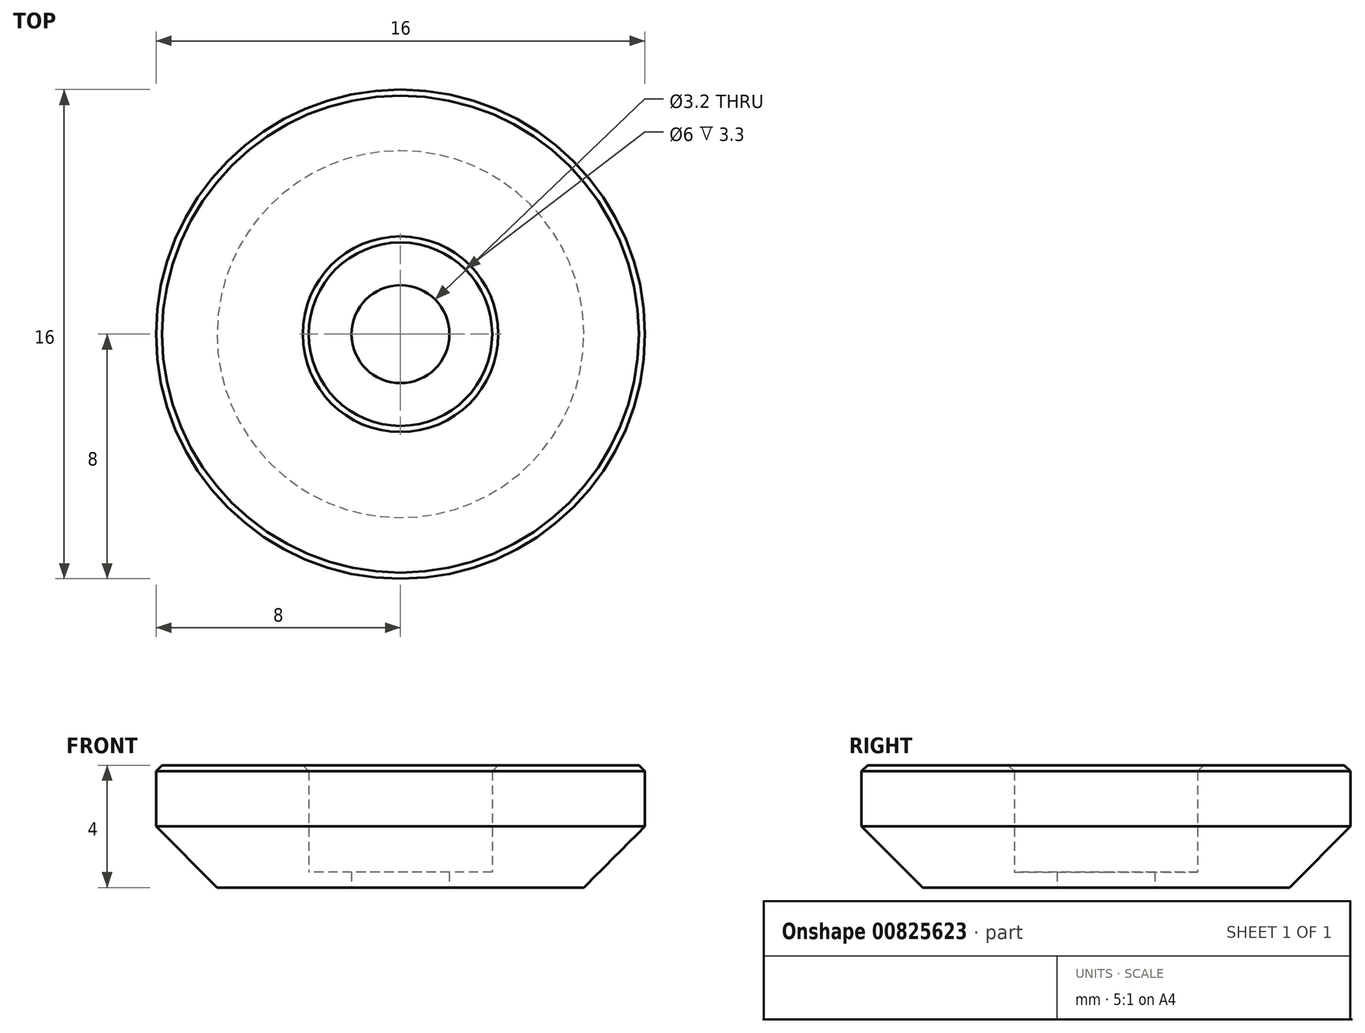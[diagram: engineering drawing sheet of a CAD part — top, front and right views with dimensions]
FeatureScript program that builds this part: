
annotation { "Feature Type Name" : "Feature", "Feature Type Description" : "" }
export const myFeature = defineFeature(function(context is Context, id is Id, definition is map)
    precondition{}
    {
        {
            var Q0;
            Q0=qCreatedBy(makeId("Top.planeOp"),FACE);
            var sketch = newSketch(context, id + "F0", { "sketchPlane" : qUnion([Q0])});
            skCircle(sketch, "E0", {"center": v(0, 0) * mm, "radius": 3 * mm});
            skCircle(sketch, "E1", {"center": v(0, 0) * mm, "radius": 1.6 * mm});
            skCircle(sketch, "E2", {"center": v(0, 0) * mm, "radius": 8 * mm});
            skSolve(sketch);
        }
        {
            var Q0;
            Q0=makeQuery(id+"F0.imprint","IMPRINT",FACE,{"disambiguationData":[TD([[makeQuery(id+"F0.imprint","IMPRINT",EDGE,{"derivedFrom":sQuery(id+"F0.wireOp",EDGE,"E0")}),1.0]])]});
            extrude(context, id + "F1", {"entities" : qUnion([Q0]), "depth" : 0.5 * mm, "offsetDistance" : 25 * mm});
        }
        {
            var Q0;
            Q0=makeQuery(id+"F0.imprint","IMPRINT",FACE,{"disambiguationData":[TD([[makeQuery(id+"F0.imprint","IMPRINT",EDGE,{"derivedFrom":sQuery(id+"F0.wireOp",EDGE,"E0")}),-1.0]])]});
            extrude(context, id + "F2", {"entities" : qUnion([Q0]), "operationType" : NewBodyOperationType.ADD, "depth" : 4 * mm, "offsetDistance" : 25 * mm});
        }
        {
            var Q0;
            Q0=makeQuery(id+"F2.opExtrude","CAP_EDGE",EDGE,{"disambiguationData":[OSD([sQuery(id+"F0.wireOp",EDGE,"E2")])],"isStart":true});
            chamfer(context, id + "F3", {"entities" : qUnion([Q0]), "width" : 2 * mm, "tangentPropagation" : true});
        }
        {
            var Q0;
            Q0=makeQuery(id+"F2.opExtrude","CAP_EDGE",EDGE,{"disambiguationData":[OSD([sQuery(id+"F0.wireOp",EDGE,"E2")])],"isStart":false});
            var Q1;
            Q1=makeQuery(id+"F2.opExtrude","CAP_EDGE",EDGE,{"disambiguationData":[OSD([sQuery(id+"F0.wireOp",EDGE,"E0")])],"isStart":false});
            var Q2;
            Q2=makeQuery(id+"F1.opExtrude","CAP_EDGE",EDGE,{"disambiguationData":[OSD([sQuery(id+"F0.wireOp",EDGE,"E0")])],"isStart":false});
            chamfer(context, id + "F4", {"entities" : qUnion([Q0, Q1, Q2]), "width" : 0.2 * mm, "tangentPropagation" : true});
        }
    });
